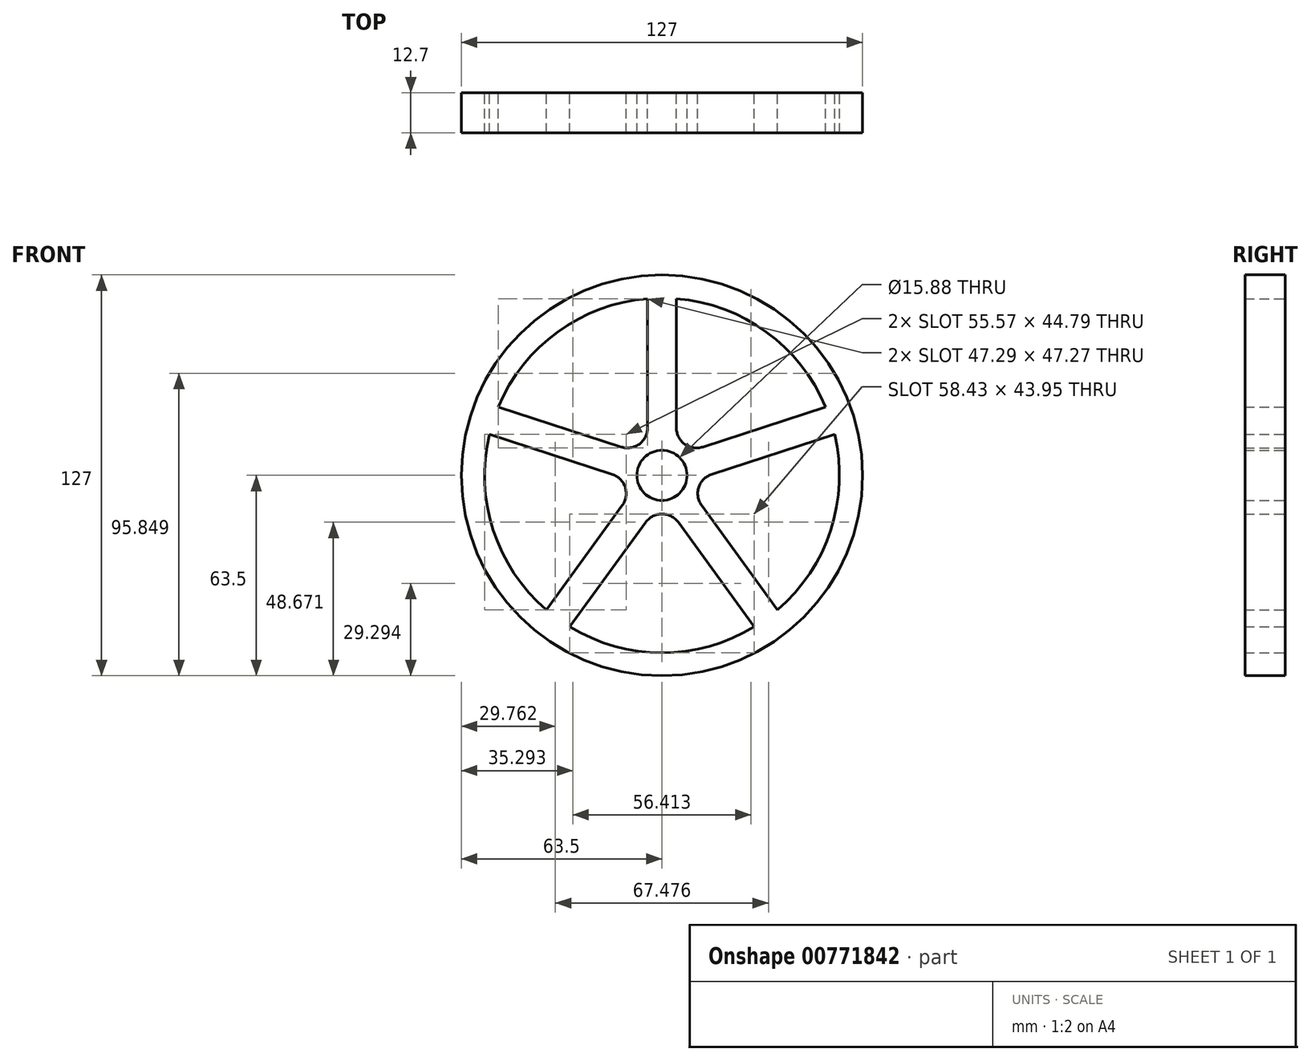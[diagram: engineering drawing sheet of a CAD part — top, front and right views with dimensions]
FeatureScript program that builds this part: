
annotation { "Feature Type Name" : "Feature", "Feature Type Description" : "" }
export const myFeature = defineFeature(function(context is Context, id is Id, definition is map)
    precondition{}
    {
        {
            var Q0;
            Q0=qCreatedBy(makeId("Front.planeOp"),FACE);
            var sketch = newSketch(context, id + "F0", { "sketchPlane" : qUnion([Q0])});
            skCircle(sketch, "E0", {"center": v(0, 0) * mm, "radius": 63.5 * mm});
            skCircle(sketch, "E1", {"center": v(0, 0) * mm, "radius": 56.18 * mm});
            skCircle(sketch, "E2.cCircle", {"center": v(0, 0) * mm, "radius": 56.18 * mm, "construction": true});
            skLineSegment(sketch, "E3", {"start": v(-51.84, 21.65) * mm, "end": v(-12.88, 9) * mm});
            skLineSegment(sketch, "E4", {"start": v(-4.57, 56) * mm, "end": v(-4.57, 15.03) * mm});
            skLineSegment(sketch, "E5", {"start": v(-15.7, 0.3) * mm, "end": v(-54.67, 12.96) * mm});
            skLineSegment(sketch, "E6", {"start": v(4.57, 15.03) * mm, "end": v(4.57, 56) * mm});
            skLineSegment(sketch, "E7", {"start": v(51.84, 21.65) * mm, "end": v(12.88, 9) * mm});
            skLineSegment(sketch, "E8", {"start": v(15.7, 0.3) * mm, "end": v(54.67, 12.96) * mm});
            skLineSegment(sketch, "E9", {"start": v(12.53, -9.47) * mm, "end": v(36.61, -42.61) * mm});
            skLineSegment(sketch, "E10", {"start": v(29.21, -47.99) * mm, "end": v(5.14, -14.85) * mm});
            skLineSegment(sketch, "E11", {"start": v(-5.14, -14.85) * mm, "end": v(-29.21, -47.99) * mm});
            skLineSegment(sketch, "E12", {"start": v(-36.61, -42.61) * mm, "end": v(-12.53, -9.47) * mm});
            skCircle(sketch, "E13", {"center": v(0, 0) * mm, "radius": 7.94 * mm});
            skArc(sketch, "E14.filletArc", {"start": v(-12.88, 9) * mm, "mid": v(-7.19, 9.9) * mm, "end": v(-4.57, 15.03) * mm});
            skArc(sketch, "E15.filletArc", {"start": v(4.57, 15.03) * mm, "mid": v(7.19, 9.9) * mm, "end": v(12.88, 9) * mm});
            skArc(sketch, "E16.filletArc", {"start": v(15.7, 0.3) * mm, "mid": v(11.63, -3.78) * mm, "end": v(12.53, -9.47) * mm});
            skArc(sketch, "E17.filletArc", {"start": v(5.14, -14.85) * mm, "mid": v(0, -12.23) * mm, "end": v(-5.14, -14.85) * mm});
            skPoint(sketch, "E18.newPointB", {"position": v(-14.8, 0) * mm});
            skArc(sketch, "E18.filletArc", {"start": v(-12.53, -9.47) * mm, "mid": v(-11.63, -3.78) * mm, "end": v(-15.7, 0.3) * mm});
            skCircle(sketch, "E19", {"center": v(-13.25, -31.42) * mm, "radius": 3.18 * mm});
            skSolve(sketch);
        }
        {
            var Q0;
            Q0 = qSketchRegion(id + "F0", true);
            var Q1;
            {var subQ2=sQuery(id+"F0.wireOp",EDGE,"E3");Q1=makeQuery(id+"F0.imprint","IMPRINT",FACE,{"disambiguationData":[TD([[makeQuery(id+"F0.imprint","IMPRINT",EDGE,{"derivedFrom":subQ2}),-1.0]])]});}
            extrude(context, id + "F1", {"entities" : qUnion([Q0, Q1]), "depth" : 12.7 * mm, "offsetDistance" : 25.4 * mm});
        }
    });
